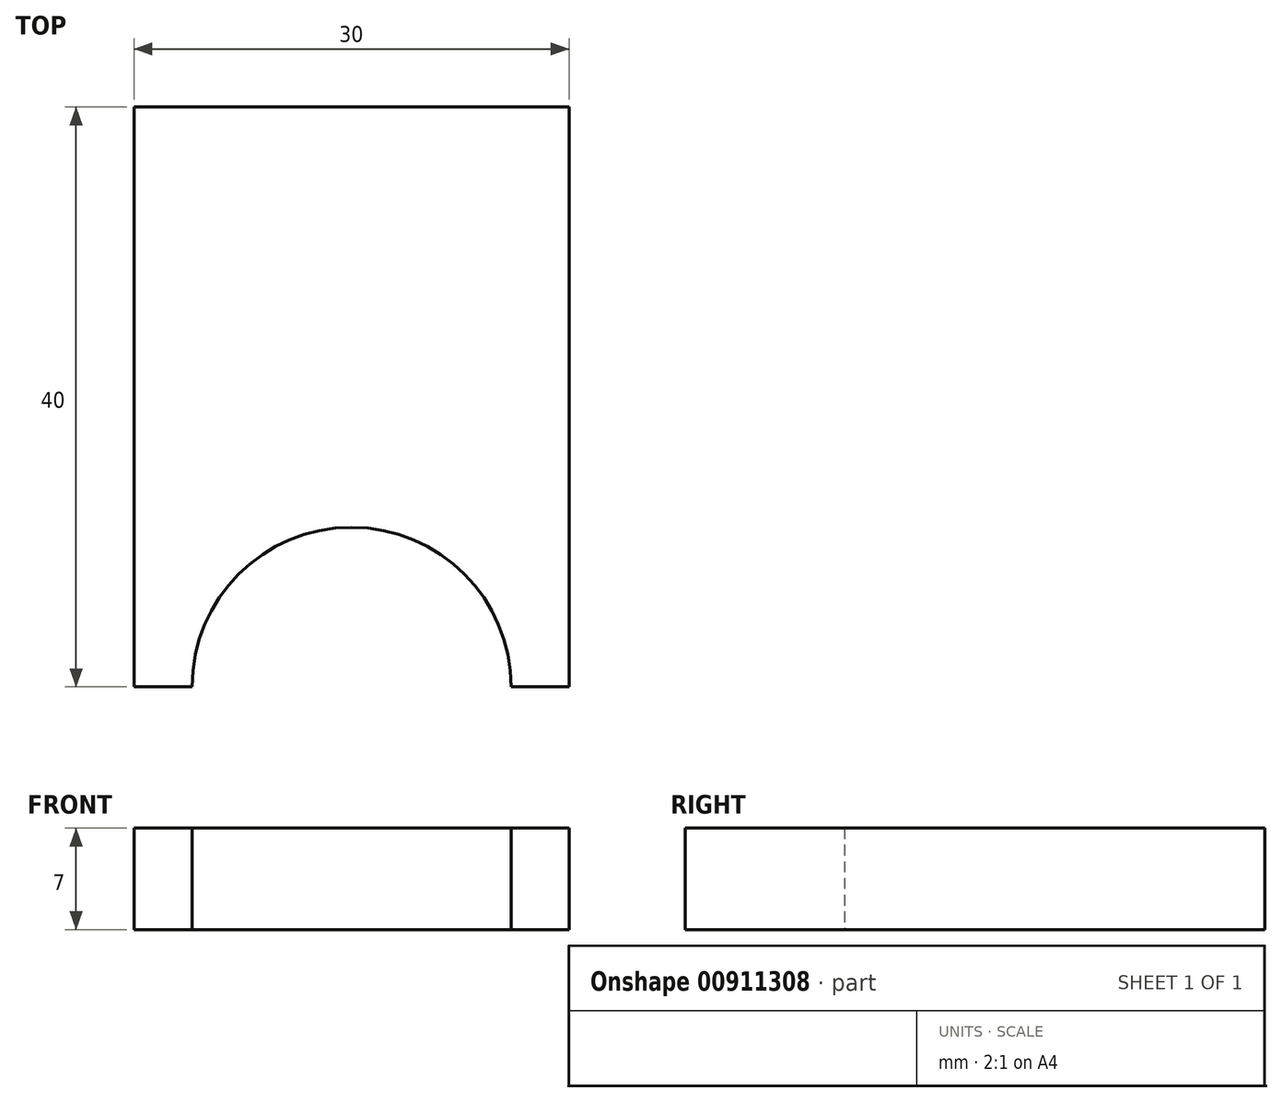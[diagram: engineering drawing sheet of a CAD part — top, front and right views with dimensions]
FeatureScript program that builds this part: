
annotation { "Feature Type Name" : "Feature", "Feature Type Description" : "" }
export const myFeature = defineFeature(function(context is Context, id is Id, definition is map)
    precondition{}
    {
        {
            var Q0;
            Q0=qCreatedBy(makeId("Top.planeOp"),FACE);
            var sketch = newSketch(context, id + "F0", { "sketchPlane" : qUnion([Q0])});
            skCircle(sketch, "E0", {"center": v(0, 0) * mm, "radius": 11 * mm});
            skLineSegment(sketch, "E1", {"start": v(0, 11) * mm, "end": v(0, 40) * mm});
            skLineSegment(sketch, "E2", {"start": v(0, 40) * mm, "end": v(15, 40) * mm});
            skLineSegment(sketch, "E3", {"start": v(15, 40) * mm, "end": v(15, 0) * mm});
            skLineSegment(sketch, "E4", {"start": v(15, 0) * mm, "end": v(0, 0) * mm});
            skLineSegment(sketch, "E5", {"start": v(0, 0) * mm, "end": v(-15, 0) * mm});
            skLineSegment(sketch, "E6", {"start": v(-15, 0) * mm, "end": v(-15, 40) * mm});
            skLineSegment(sketch, "E7", {"start": v(-15, 40) * mm, "end": v(0, 40) * mm});
            skSolve(sketch);
        }
        {
            var Q0;
            {var subQ4=sQuery(id+"F0.wireOp",EDGE,"E1");Q0=makeQuery(id+"F0.imprint","IMPRINT",FACE,{"disambiguationData":[TD([[makeQuery(id+"F0.imprint","IMPRINT",EDGE,{"derivedFrom":subQ4}),1.0]])]});}
            var Q1;
            {var subQ0=sQuery(id+"F0.wireOp",EDGE,"E1");Q1=makeQuery(id+"F0.imprint","IMPRINT",FACE,{"disambiguationData":[TD([[makeQuery(id+"F0.imprint","IMPRINT",EDGE,{"derivedFrom":subQ0}),-1.0]])]});}
            extrude(context, id + "F1", {"entities" : qUnion([Q0, Q1]), "depth" : 7 * mm, "offsetDistance" : 25 * mm});
        }
    });
